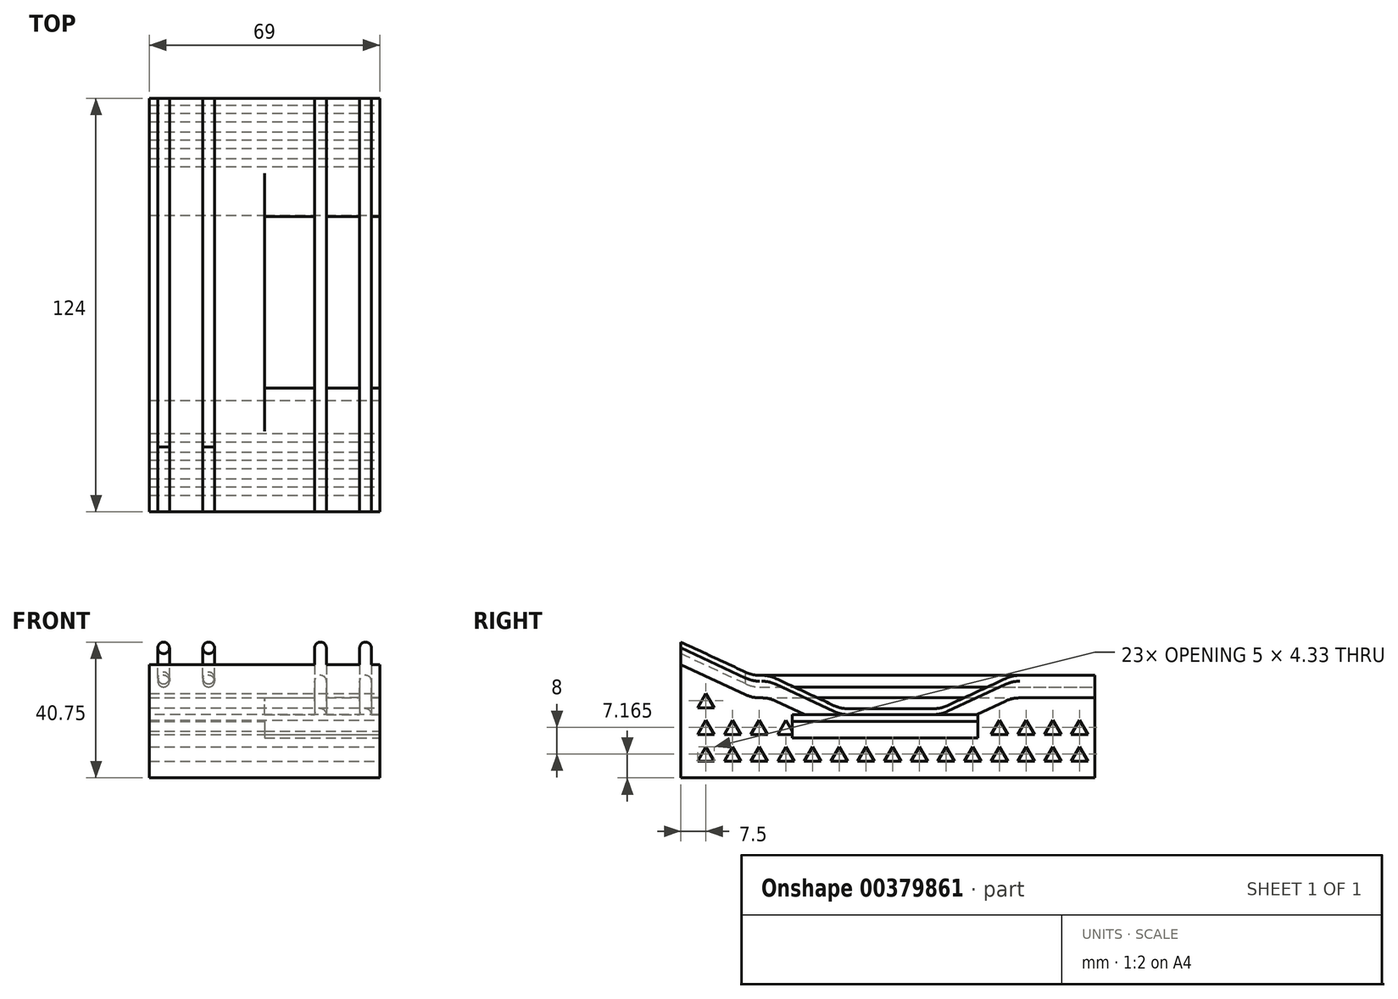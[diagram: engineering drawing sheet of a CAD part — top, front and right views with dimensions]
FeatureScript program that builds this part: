
annotation { "Feature Type Name" : "Feature", "Feature Type Description" : "" }
export const myFeature = defineFeature(function(context is Context, id is Id, definition is map)
    precondition{}
    {
        {
            var Q0;
            Q0=qCreatedBy(makeId("Front.planeOp"),FACE);
            var sketch = newSketch(context, id + "F0", { "sketchPlane" : qUnion([Q0])});
            skLineSegment(sketch, "E0.bottom", {"start": v(-34.5, 10) * mm, "end": v(34.5, 10) * mm});
            skLineSegment(sketch, "E0.top", {"start": v(-34.5, 0) * mm, "end": v(34.5, 0) * mm});
            skLineSegment(sketch, "E0.left", {"start": v(-34.5, 10) * mm, "end": v(-34.5, 0) * mm});
            skLineSegment(sketch, "E0.right", {"start": v(34.5, 10) * mm, "end": v(34.5, 0) * mm});
            skLineSegment(sketch, "E1.bottom", {"start": v(-32, 10) * mm, "end": v(-28.5, 10) * mm});
            skLineSegment(sketch, "E1.top", {"start": v(-32, 15) * mm, "end": v(-28.5, 15) * mm});
            skLineSegment(sketch, "E1.left", {"start": v(-32, 10) * mm, "end": v(-32, 15) * mm});
            skLineSegment(sketch, "E1.right", {"start": v(-28.5, 10) * mm, "end": v(-28.5, 15) * mm});
            skLineSegment(sketch, "E2.bottom", {"start": v(-18.5, 10) * mm, "end": v(-15, 10) * mm});
            skLineSegment(sketch, "E2.top", {"start": v(-18.5, 15) * mm, "end": v(-15, 15) * mm});
            skLineSegment(sketch, "E2.left", {"start": v(-18.5, 10) * mm, "end": v(-18.5, 15) * mm});
            skLineSegment(sketch, "E2.right", {"start": v(-15, 10) * mm, "end": v(-15, 15) * mm});
            skLineSegment(sketch, "E3.MirrorCS", {"start": v(15, 10) * mm, "end": v(15, 15) * mm});
            skLineSegment(sketch, "E4.MirrorCS", {"start": v(18.5, 15) * mm, "end": v(15, 15) * mm});
            skLineSegment(sketch, "E5.MirrorCS", {"start": v(18.5, 10) * mm, "end": v(18.5, 15) * mm});
            skLineSegment(sketch, "E6.MirrorCS", {"start": v(28.5, 10) * mm, "end": v(28.5, 15) * mm});
            skLineSegment(sketch, "E7.MirrorCS", {"start": v(32, 15) * mm, "end": v(28.5, 15) * mm});
            skLineSegment(sketch, "E8.MirrorCS", {"start": v(32, 10) * mm, "end": v(32, 15) * mm});
            skCircle(sketch, "E9", {"center": v(-30.25, 15) * mm, "radius": 1.75 * mm});
            skCircle(sketch, "E10", {"center": v(-16.75, 15) * mm, "radius": 1.75 * mm});
            skCircle(sketch, "E11.MirrorC", {"center": v(16.75, 15) * mm, "radius": 1.75 * mm});
            skCircle(sketch, "E12.MirrorC", {"center": v(30.25, 15) * mm, "radius": 1.75 * mm});
            skLineSegment(sketch, "E13.top", {"start": v(-34.5, -24) * mm, "end": v(34.5, -24) * mm});
            skLineSegment(sketch, "E13.left", {"start": v(-34.5, 0) * mm, "end": v(-34.5, -24) * mm});
            skLineSegment(sketch, "E13.right", {"start": v(34.5, 0) * mm, "end": v(34.5, -24) * mm});
            skLineSegment(sketch, "E14", {"start": v(0, 0) * mm, "end": v(0, 10) * mm});
            skLineSegment(sketch, "E15", {"start": v(34.5, -5) * mm, "end": v(-34.5, -5) * mm});
            skLineSegment(sketch, "E16", {"start": v(-34.5, -12) * mm, "end": v(34.5, -12) * mm});
            skLineSegment(sketch, "E17", {"start": v(-34.5, -7) * mm, "end": v(0, -7) * mm});
            skLineSegment(sketch, "E18", {"start": v(0, -7) * mm, "end": v(0, -12) * mm});
            skSolve(sketch);
        }
        {
            var Q0;
            Q0=qCreatedBy(makeId("Right.planeOp"),FACE);
            var sketch = newSketch(context, id + "F1", { "sketchPlane" : qUnion([Q0])});
            skLineSegment(sketch, "E19", {"start": v(0, 0) * mm, "end": v(19.44, -9.06) * mm});
            skLineSegment(sketch, "E20", {"start": v(101.55, -10) * mm, "end": v(124, -10) * mm, "construction": true});
            skLineSegment(sketch, "E21", {"start": v(28.45, -10.94) * mm, "end": v(45.88, -19.06) * mm});
            skLineSegment(sketch, "E22", {"start": v(50.1, -20) * mm, "end": v(75.67, -20) * mm});
            skLineSegment(sketch, "E23", {"start": v(79.9, -19.06) * mm, "end": v(97.33, -10.94) * mm});
            skLineSegment(sketch, "E24", {"start": v(124, -10) * mm, "end": v(124, -20) * mm, "construction": true});
            skLineSegment(sketch, "E25.MirrorCS", {"start": v(248, 0) * mm, "end": v(226.55, -10) * mm});
            skLineSegment(sketch, "E26.MirrorCS", {"start": v(221.55, -10) * mm, "end": v(200.1, -20) * mm});
            skLineSegment(sketch, "E27.MirrorCS", {"start": v(170.1, -20) * mm, "end": v(147.37, -9.4) * mm});
            skLineSegment(sketch, "E28.MirrorCS", {"start": v(226.55, -10) * mm, "end": v(124, -10) * mm});
            skLineSegment(sketch, "E29.MirrorCS", {"start": v(200.1, -20) * mm, "end": v(170.1, -20) * mm});
            skLineSegment(sketch, "E30", {"start": v(23.66, -10) * mm, "end": v(24.23, -10) * mm});
            skLineSegment(sketch, "E31", {"start": v(101.55, -10) * mm, "end": v(124, -10) * mm});
            skPoint(sketch, "E32.visualSharp", {"position": v(26.45, -10) * mm});
            skArc(sketch, "E32.filletArc", {"start": v(28.45, -10.94) * mm, "mid": v(26.4, -10.24) * mm, "end": v(24.23, -10) * mm});
            skPoint(sketch, "E33.visualSharp", {"position": v(21.45, -10) * mm});
            skArc(sketch, "E33.filletArc", {"start": v(19.44, -9.06) * mm, "mid": v(21.5, -9.76) * mm, "end": v(23.66, -10) * mm});
            skPoint(sketch, "E34.visualSharp", {"position": v(47.9, -20) * mm});
            skArc(sketch, "E34.filletArc", {"start": v(45.88, -19.06) * mm, "mid": v(47.94, -19.76) * mm, "end": v(50.1, -20) * mm});
            skPoint(sketch, "E35.visualSharp", {"position": v(77.9, -20) * mm});
            skArc(sketch, "E35.filletArc", {"start": v(75.67, -20) * mm, "mid": v(77.84, -19.76) * mm, "end": v(79.9, -19.06) * mm});
            skLineSegment(sketch, "E36", {"start": v(24.23, -10) * mm, "end": v(124, -10) * mm});
            skArc(sketch, "E37.filletArc", {"start": v(101.55, -10) * mm, "mid": v(99.39, -10.24) * mm, "end": v(97.33, -10.94) * mm});
            skSolve(sketch);
        }
        {
            var Q0;
            {var subQ0=sQuery(id+"F0.wireOp",EDGE,"E0.left");Q0=makeQuery(id+"F0.imprint","IMPRINT",FACE,{"disambiguationData":[TD([[makeQuery(id+"F0.imprint","IMPRINT",EDGE,{"derivedFrom":subQ0}),1.0]])]});}
            var Q1;
            Q1=makeQuery(id+"F0.imprint","IMPRINT",FACE,{"disambiguationData":[TD([[makeQuery(id+"F0.imprint","IMPRINT",EDGE,{"derivedFrom":sQuery(id+"F0.wireOp",EDGE,"E1.bottom")}),1.0]])]});
            var Q2;
            Q2=makeQuery(id+"F0.imprint","IMPRINT",FACE,{"disambiguationData":[TD([[makeQuery(id+"F0.imprint","IMPRINT",EDGE,{"derivedFrom":sQuery(id+"F0.wireOp",EDGE,"E2.bottom")}),1.0]])]});
            var Q3;
            {var subQ0=sQuery(id+"F0.wireOp",EDGE,"E1.top");Q3=makeQuery(id+"F0.imprint","IMPRINT",FACE,{"disambiguationData":[TD([[makeQuery(id+"F0.imprint","IMPRINT",EDGE,{"derivedFrom":subQ0}),1.0]])]});}
            var Q4;
            {var subQ0=sQuery(id+"F0.wireOp",EDGE,"E2.top");Q4=makeQuery(id+"F0.imprint","IMPRINT",FACE,{"disambiguationData":[TD([[makeQuery(id+"F0.imprint","IMPRINT",EDGE,{"derivedFrom":subQ0}),1.0]])]});}
            var Q5;
            {var subQ0=sQuery(id+"F0.wireOp",EDGE,"E1.top");Q5=makeQuery(id+"F0.imprint","IMPRINT",FACE,{"disambiguationData":[TD([[makeQuery(id+"F0.imprint","IMPRINT",EDGE,{"derivedFrom":subQ0}),-1.0]])]});}
            var Q6;
            {var subQ0=sQuery(id+"F0.wireOp",EDGE,"E2.top");Q6=makeQuery(id+"F0.imprint","IMPRINT",FACE,{"disambiguationData":[TD([[makeQuery(id+"F0.imprint","IMPRINT",EDGE,{"derivedFrom":subQ0}),-1.0]])]});}
            var Q7;
            Q7=sQuery(id+"F1.wireOp",EDGE,"E19");
            var Q8;
            Q8=sQuery(id+"F1.wireOp",EDGE,"E33.filletArc");
            var Q9;
            Q9=sQuery(id+"F1.wireOp",EDGE,"E30");
            var Q10;
            Q10=sQuery(id+"F1.wireOp",EDGE,"E36");
            sweep(context, id + "F2", {"profiles" : qUnion([Q0, Q1, Q2, Q3, Q4, Q5, Q6]), "path" : qUnion([Q7, Q8, Q9, Q10]), "keepProfileOrientation" : true});
        }
        {
            var Q0;
            {var subQ0=sQuery(id+"F0.wireOp",EDGE,"E4.MirrorCS");Q0=makeQuery(id+"F0.imprint","IMPRINT",FACE,{"disambiguationData":[TD([[makeQuery(id+"F0.imprint","IMPRINT",EDGE,{"derivedFrom":subQ0}),-1.0]])]});}
            var Q1;
            {var subQ0=sQuery(id+"F0.wireOp",EDGE,"E7.MirrorCS");Q1=makeQuery(id+"F0.imprint","IMPRINT",FACE,{"disambiguationData":[TD([[makeQuery(id+"F0.imprint","IMPRINT",EDGE,{"derivedFrom":subQ0}),-1.0]])]});}
            var Q2;
            {var subQ0=sQuery(id+"F0.wireOp",EDGE,"E3.MirrorCS");Q2=makeQuery(id+"F0.imprint","IMPRINT",FACE,{"disambiguationData":[TD([[makeQuery(id+"F0.imprint","IMPRINT",EDGE,{"derivedFrom":subQ0}),-1.0]])]});}
            var Q3;
            {var subQ0=sQuery(id+"F0.wireOp",EDGE,"E6.MirrorCS");Q3=makeQuery(id+"F0.imprint","IMPRINT",FACE,{"disambiguationData":[TD([[makeQuery(id+"F0.imprint","IMPRINT",EDGE,{"derivedFrom":subQ0}),-1.0]])]});}
            var Q4;
            {var subQ0=sQuery(id+"F0.wireOp",EDGE,"E4.MirrorCS");Q4=makeQuery(id+"F0.imprint","IMPRINT",FACE,{"disambiguationData":[TD([[makeQuery(id+"F0.imprint","IMPRINT",EDGE,{"derivedFrom":subQ0}),1.0]])]});}
            var Q5;
            {var subQ0=sQuery(id+"F0.wireOp",EDGE,"E7.MirrorCS");Q5=makeQuery(id+"F0.imprint","IMPRINT",FACE,{"disambiguationData":[TD([[makeQuery(id+"F0.imprint","IMPRINT",EDGE,{"derivedFrom":subQ0}),1.0]])]});}
            var Q6;
            {var subQ6=sQuery(id+"F0.wireOp",EDGE,"E0.right");Q6=makeQuery(id+"F0.imprint","IMPRINT",FACE,{"disambiguationData":[TD([[makeQuery(id+"F0.imprint","IMPRINT",EDGE,{"derivedFrom":subQ6}),-1.0]])]});}
            var Q7;
            Q7=sQuery(id+"F1.wireOp",EDGE,"E19");
            var Q8;
            Q8=sQuery(id+"F1.wireOp",EDGE,"E33.filletArc");
            var Q9;
            Q9=sQuery(id+"F1.wireOp",EDGE,"E30");
            var Q10;
            Q10=sQuery(id+"F1.wireOp",EDGE,"E32.filletArc");
            var Q11;
            Q11=sQuery(id+"F1.wireOp",EDGE,"E21");
            var Q12;
            Q12=sQuery(id+"F1.wireOp",EDGE,"E34.filletArc");
            sweep(context, id + "F3", {"operationType" : NewBodyOperationType.ADD, "profiles" : qUnion([Q0, Q1, Q2, Q3, Q4, Q5, Q6]), "path" : qUnion([Q7, Q8, Q9, Q10, Q11, Q12]), "keepProfileOrientation" : true});
        }
        {
            var Q0;
            Q0=makeQuery(id+"F3.opSweep","CAP_FACE",FACE,{"disambiguationData":[OSD([sQuery(id+"F0.wireOp",EDGE,"E0.bottom"),sQuery(id+"F0.wireOp",EDGE,"E0.right"),sQuery(id+"F0.wireOp",EDGE,"E3.MirrorCS"),sQuery(id+"F0.wireOp",EDGE,"E5.MirrorCS"),sQuery(id+"F0.wireOp",EDGE,"E6.MirrorCS"),sQuery(id+"F0.wireOp",EDGE,"E8.MirrorCS"),sQuery(id+"F0.wireOp",EDGE,"E11.MirrorC"),sQuery(id+"F0.wireOp",EDGE,"E12.MirrorC"),sQuery(id+"F0.wireOp",EDGE,"E0.top"),sQuery(id+"F0.wireOp",EDGE,"E14"),sQuery(id+"F1.wireOp",VERTEX,"E34.filletArc.end")])],"isStart":false});
            var Q1;
            Q1=sQuery(id+"F1.wireOp",EDGE,"E22");
            var Q2;
            Q2=sQuery(id+"F1.wireOp",EDGE,"E35.filletArc");
            var Q3;
            Q3=sQuery(id+"F1.wireOp",EDGE,"E23");
            var Q4;
            Q4=sQuery(id+"F1.wireOp",EDGE,"E31");
            var Q5;
            Q5=sQuery(id+"F1.wireOp",EDGE,"E37.filletArc");
            sweep(context, id + "F4", {"profiles" : qUnion([Q0]), "path" : qUnion([Q1, Q2, Q3, Q4, Q5]), "keepProfileOrientation" : true});
        }
        {
            var Q0;
            Q0=makeQuery(id+"F0.imprint","IMPRINT",FACE,{"disambiguationData":[TD([[makeQuery(id+"F0.imprint","IMPRINT",EDGE,{"derivedFrom":sQuery(id+"F0.wireOp",EDGE,"E13.top")}),1.0]])]});
            var Q1;
            {var subQ0=sQuery(id+"F0.wireOp",EDGE,"E15");Q1=makeQuery(id+"F0.imprint","IMPRINT",FACE,{"disambiguationData":[TD([[makeQuery(id+"F0.imprint","IMPRINT",EDGE,{"derivedFrom":subQ0}),1.0]])]});}
            var Q2;
            {var subQ3=sQuery(id+"F0.wireOp",EDGE,"E17");Q2=makeQuery(id+"F0.imprint","IMPRINT",FACE,{"disambiguationData":[TD([[makeQuery(id+"F0.imprint","IMPRINT",EDGE,{"derivedFrom":subQ3}),-1.0]])]});}
            extrude(context, id + "F5", {"entities" : qUnion([Q0, Q1, Q2]), "oppositeDirection" : true, "depth" : 124 * mm});
        }
        {
            var Q0;
            {var subQ0=sQuery(id+"F0.wireOp",EDGE,"E15");Q0=makeQuery(id+"F0.imprint","IMPRINT",FACE,{"disambiguationData":[TD([[makeQuery(id+"F0.imprint","IMPRINT",EDGE,{"derivedFrom":subQ0}),1.0]])]});}
            extrude(context, id + "F6", {"entities" : qUnion([Q0]), "operationType" : NewBodyOperationType.REMOVE, "oppositeDirection" : true, "depth" : 89 * mm});
        }
        {
            var Q0;
            {var subQ0=sQuery(id+"F0.wireOp",EDGE,"E15");Q0=makeQuery(id+"F0.imprint","IMPRINT",FACE,{"disambiguationData":[TD([[makeQuery(id+"F0.imprint","IMPRINT",EDGE,{"derivedFrom":subQ0}),1.0]])]});}
            extrude(context, id + "F7", {"entities" : qUnion([Q0]), "operationType" : NewBodyOperationType.ADD, "oppositeDirection" : true, "depth" : 33.4 * mm});
        }
        {
            var Q0;
            {var subQ3=sQuery(id+"F0.wireOp",EDGE,"E15");Q0=makeQuery(id+"F0.imprint","IMPRINT",FACE,{"disambiguationData":[TD([[makeQuery(id+"F0.imprint","IMPRINT",EDGE,{"derivedFrom":subQ3}),-1.0]])]});}
            extrude(context, id + "F8", {"entities" : qUnion([Q0]), "operationType" : NewBodyOperationType.ADD, "oppositeDirection" : true, "depth" : 15 * mm});
        }
        {
            var Q0;
            Q0=makeQuery(id+"F2.opSweep","SWEPT_BODY",BODY,{"disambiguationData":[OSD([sQuery(id+"F0.wireOp",EDGE,"E0.bottom"),sQuery(id+"F0.wireOp",EDGE,"E0.left"),sQuery(id+"F0.wireOp",EDGE,"E1.left"),sQuery(id+"F0.wireOp",EDGE,"E1.right"),sQuery(id+"F0.wireOp",EDGE,"E2.left"),sQuery(id+"F0.wireOp",EDGE,"E2.right"),sQuery(id+"F0.wireOp",EDGE,"E9"),sQuery(id+"F0.wireOp",EDGE,"E10"),sQuery(id+"F0.wireOp",EDGE,"E0.top"),sQuery(id+"F0.wireOp",EDGE,"E14"),sQuery(id+"F1.wireOp",EDGE,"E20")])]});
            var Q1;
            Q1=makeQuery(id+"F5.opExtrude","SWEPT_BODY",BODY,{"disambiguationData":[OSD([sQuery(id+"F0.wireOp",EDGE,"E13.top"),sQuery(id+"F0.wireOp",EDGE,"E13.left"),sQuery(id+"F0.wireOp",EDGE,"E13.right"),sQuery(id+"F0.wireOp",EDGE,"E15")])]});
            var Q2;
            Q2=makeQuery(id+"F4.opSweep","SWEPT_BODY",BODY,{"disambiguationData":[OSD([sQuery(id+"F0.wireOp",EDGE,"E0.bottom"),sQuery(id+"F0.wireOp",EDGE,"E0.right"),sQuery(id+"F0.wireOp",EDGE,"E3.MirrorCS"),sQuery(id+"F0.wireOp",EDGE,"E5.MirrorCS"),sQuery(id+"F0.wireOp",EDGE,"E6.MirrorCS"),sQuery(id+"F0.wireOp",EDGE,"E8.MirrorCS"),sQuery(id+"F0.wireOp",EDGE,"E11.MirrorC"),sQuery(id+"F0.wireOp",EDGE,"E12.MirrorC"),sQuery(id+"F0.wireOp",EDGE,"E0.top"),sQuery(id+"F0.wireOp",EDGE,"E14"),sQuery(id+"F1.wireOp",VERTEX,"E34.filletArc.end"),sQuery(id+"F1.wireOp",EDGE,"E22")])]});
            booleanBodies(context, id + "F9", {"operationType" : BooleanOperationType.UNION, "tools" : qUnion([Q0, Q1, Q2])});
        }
        {
            var Q0;
            {var subQ0=sQuery(id+"F0.wireOp",EDGE,"E13.right");Q0=makeQuery(id+"F9.opBoolean","MERGE",FACE,{"derivedFrom":[makeQuery(id+"Fo5E0ju6kwFAIzG_1.boolean.opBoolean","MERGE",FACE,{"derivedFrom":[makeQuery(id+"F3.opSweep","SWEPT_FACE",FACE,{"disambiguationData":[OSD([sQuery(id+"F0.wireOp",EDGE,"E0.right"),sQuery(id+"F1.wireOp",EDGE,"E19")])]}),makeQuery(id+"Fo5E0ju6kwFAIzG_1.opExtrude","SWEPT_FACE",FACE,{"disambiguationData":[OSD([sQuery(id+"FUxDlczvYnfELys.wireOp",EDGE,"94261386-e1e3-4ee6-9ad5-568f97032458.right")])]})]}),makeQuery(id+"F8.boolean.opBoolean","MERGE",FACE,{"derivedFrom":[makeQuery(id+"F7.boolean.opBoolean","MERGE",FACE,{"derivedFrom":[makeQuery(id+"F5.opExtrude","SWEPT_FACE",FACE,{"disambiguationData":[OSD([subQ0])]}),makeQuery(id+"F7.opExtrude","SWEPT_FACE",FACE,{"disambiguationData":[OSD([subQ0])]})]}),makeQuery(id+"F8.opExtrude","SWEPT_FACE",FACE,{"disambiguationData":[OSD([subQ0])]})]})]});}
            var sketch = newSketch(context, id + "F10", { "sketchPlane" : qUnion([Q0])});
            skLineSegment(sketch, "E38", {"start": v(5, -19) * mm, "end": v(7.5, -14.67) * mm});
            skLineSegment(sketch, "E39", {"start": v(7.5, -14.67) * mm, "end": v(10, -19) * mm});
            skLineSegment(sketch, "E40", {"start": v(10, -19) * mm, "end": v(5, -19) * mm});
            skLineSegment(sketch, "E41.0.1.0", {"start": v(5, -11) * mm, "end": v(7.5, -6.67) * mm});
            skLineSegment(sketch, "E41.0.1.1", {"start": v(7.5, -6.67) * mm, "end": v(10, -11) * mm});
            skLineSegment(sketch, "E41.0.1.2", {"start": v(10, -11) * mm, "end": v(5, -11) * mm});
            skLineSegment(sketch, "E41.0.2.0", {"start": v(5, -3) * mm, "end": v(7.5, 1.33) * mm});
            skLineSegment(sketch, "E41.0.2.1", {"start": v(7.5, 1.33) * mm, "end": v(10, -3) * mm});
            skLineSegment(sketch, "E41.0.2.2", {"start": v(10, -3) * mm, "end": v(5, -3) * mm});
            skLineSegment(sketch, "E41.1.0.0", {"start": v(13, -19) * mm, "end": v(15.5, -14.67) * mm});
            skLineSegment(sketch, "E41.1.0.1", {"start": v(15.5, -14.67) * mm, "end": v(18, -19) * mm});
            skLineSegment(sketch, "E41.1.0.2", {"start": v(18, -19) * mm, "end": v(13, -19) * mm});
            skLineSegment(sketch, "E41.1.1.0", {"start": v(13, -11) * mm, "end": v(15.5, -6.67) * mm});
            skLineSegment(sketch, "E41.1.1.1", {"start": v(15.5, -6.67) * mm, "end": v(18, -11) * mm});
            skLineSegment(sketch, "E41.1.1.2", {"start": v(18, -11) * mm, "end": v(13, -11) * mm});
            skLineSegment(sketch, "E41.1.2.0", {"start": v(13, -3) * mm, "end": v(15.5, 1.33) * mm});
            skLineSegment(sketch, "E41.1.2.1", {"start": v(15.5, 1.33) * mm, "end": v(18, -3) * mm});
            skLineSegment(sketch, "E41.1.2.2", {"start": v(18, -3) * mm, "end": v(13, -3) * mm});
            skLineSegment(sketch, "E41.2.0.0", {"start": v(21, -19) * mm, "end": v(23.5, -14.67) * mm});
            skLineSegment(sketch, "E41.2.0.1", {"start": v(23.5, -14.67) * mm, "end": v(26, -19) * mm});
            skLineSegment(sketch, "E41.2.0.2", {"start": v(26, -19) * mm, "end": v(21, -19) * mm});
            skLineSegment(sketch, "E41.2.1.0", {"start": v(21, -11) * mm, "end": v(23.5, -6.67) * mm});
            skLineSegment(sketch, "E41.2.1.1", {"start": v(23.5, -6.67) * mm, "end": v(26, -11) * mm});
            skLineSegment(sketch, "E41.2.1.2", {"start": v(26, -11) * mm, "end": v(21, -11) * mm});
            skLineSegment(sketch, "E41.2.2.0", {"start": v(21, -3) * mm, "end": v(23.5, 1.33) * mm});
            skLineSegment(sketch, "E41.2.2.1", {"start": v(23.5, 1.33) * mm, "end": v(26, -3) * mm});
            skLineSegment(sketch, "E41.2.2.2", {"start": v(26, -3) * mm, "end": v(21, -3) * mm});
            skLineSegment(sketch, "E41.3.0.0", {"start": v(29, -19) * mm, "end": v(31.5, -14.67) * mm});
            skLineSegment(sketch, "E41.3.0.1", {"start": v(31.5, -14.67) * mm, "end": v(34, -19) * mm});
            skLineSegment(sketch, "E41.3.0.2", {"start": v(34, -19) * mm, "end": v(29, -19) * mm});
            skLineSegment(sketch, "E41.3.1.0", {"start": v(29, -11) * mm, "end": v(31.5, -6.67) * mm});
            skLineSegment(sketch, "E41.3.1.1", {"start": v(31.5, -6.67) * mm, "end": v(34, -11) * mm});
            skLineSegment(sketch, "E41.3.1.2", {"start": v(34, -11) * mm, "end": v(29, -11) * mm});
            skLineSegment(sketch, "E41.3.2.0", {"start": v(29, -3) * mm, "end": v(31.5, 1.33) * mm});
            skLineSegment(sketch, "E41.3.2.1", {"start": v(31.5, 1.33) * mm, "end": v(34, -3) * mm});
            skLineSegment(sketch, "E41.3.2.2", {"start": v(34, -3) * mm, "end": v(29, -3) * mm});
            skLineSegment(sketch, "E41.4.0.0", {"start": v(37, -19) * mm, "end": v(39.5, -14.67) * mm});
            skLineSegment(sketch, "E41.4.0.1", {"start": v(39.5, -14.67) * mm, "end": v(42, -19) * mm});
            skLineSegment(sketch, "E41.4.0.2", {"start": v(42, -19) * mm, "end": v(37, -19) * mm});
            skLineSegment(sketch, "E41.4.1.0", {"start": v(37, -11) * mm, "end": v(39.5, -6.67) * mm});
            skLineSegment(sketch, "E41.4.1.1", {"start": v(39.5, -6.67) * mm, "end": v(42, -11) * mm});
            skLineSegment(sketch, "E41.4.1.2", {"start": v(42, -11) * mm, "end": v(37, -11) * mm});
            skLineSegment(sketch, "E41.4.2.0", {"start": v(37, -3) * mm, "end": v(39.5, 1.33) * mm});
            skLineSegment(sketch, "E41.4.2.1", {"start": v(39.5, 1.33) * mm, "end": v(42, -3) * mm});
            skLineSegment(sketch, "E41.4.2.2", {"start": v(42, -3) * mm, "end": v(37, -3) * mm});
            skLineSegment(sketch, "E41.5.0.0", {"start": v(45, -19) * mm, "end": v(47.5, -14.67) * mm});
            skLineSegment(sketch, "E41.5.0.1", {"start": v(47.5, -14.67) * mm, "end": v(50, -19) * mm});
            skLineSegment(sketch, "E41.5.0.2", {"start": v(50, -19) * mm, "end": v(45, -19) * mm});
            skLineSegment(sketch, "E41.5.1.0", {"start": v(45, -11) * mm, "end": v(47.5, -6.67) * mm});
            skLineSegment(sketch, "E41.5.1.1", {"start": v(47.5, -6.67) * mm, "end": v(50, -11) * mm});
            skLineSegment(sketch, "E41.5.1.2", {"start": v(50, -11) * mm, "end": v(45, -11) * mm});
            skLineSegment(sketch, "E41.5.2.0", {"start": v(45, -3) * mm, "end": v(47.5, 1.33) * mm});
            skLineSegment(sketch, "E41.5.2.1", {"start": v(47.5, 1.33) * mm, "end": v(50, -3) * mm});
            skLineSegment(sketch, "E41.5.2.2", {"start": v(50, -3) * mm, "end": v(45, -3) * mm});
            skLineSegment(sketch, "E41.6.0.0", {"start": v(53, -19) * mm, "end": v(55.5, -14.67) * mm});
            skLineSegment(sketch, "E41.6.0.1", {"start": v(55.5, -14.67) * mm, "end": v(58, -19) * mm});
            skLineSegment(sketch, "E41.6.0.2", {"start": v(58, -19) * mm, "end": v(53, -19) * mm});
            skLineSegment(sketch, "E41.6.1.0", {"start": v(53, -11) * mm, "end": v(55.5, -6.67) * mm});
            skLineSegment(sketch, "E41.6.1.1", {"start": v(55.5, -6.67) * mm, "end": v(58, -11) * mm});
            skLineSegment(sketch, "E41.6.1.2", {"start": v(58, -11) * mm, "end": v(53, -11) * mm});
            skLineSegment(sketch, "E41.6.2.0", {"start": v(53, -3) * mm, "end": v(55.5, 1.33) * mm});
            skLineSegment(sketch, "E41.6.2.1", {"start": v(55.5, 1.33) * mm, "end": v(58, -3) * mm});
            skLineSegment(sketch, "E41.6.2.2", {"start": v(58, -3) * mm, "end": v(53, -3) * mm});
            skLineSegment(sketch, "E41.7.0.0", {"start": v(61, -19) * mm, "end": v(63.5, -14.67) * mm});
            skLineSegment(sketch, "E41.7.0.1", {"start": v(63.5, -14.67) * mm, "end": v(66, -19) * mm});
            skLineSegment(sketch, "E41.7.0.2", {"start": v(66, -19) * mm, "end": v(61, -19) * mm});
            skLineSegment(sketch, "E41.7.1.0", {"start": v(61, -11) * mm, "end": v(63.5, -6.67) * mm});
            skLineSegment(sketch, "E41.7.1.1", {"start": v(63.5, -6.67) * mm, "end": v(66, -11) * mm});
            skLineSegment(sketch, "E41.7.1.2", {"start": v(66, -11) * mm, "end": v(61, -11) * mm});
            skLineSegment(sketch, "E41.7.2.0", {"start": v(61, -3) * mm, "end": v(63.5, 1.33) * mm});
            skLineSegment(sketch, "E41.7.2.1", {"start": v(63.5, 1.33) * mm, "end": v(66, -3) * mm});
            skLineSegment(sketch, "E41.7.2.2", {"start": v(66, -3) * mm, "end": v(61, -3) * mm});
            skLineSegment(sketch, "E41.8.0.0", {"start": v(69, -19) * mm, "end": v(71.5, -14.67) * mm});
            skLineSegment(sketch, "E41.8.0.1", {"start": v(71.5, -14.67) * mm, "end": v(74, -19) * mm});
            skLineSegment(sketch, "E41.8.0.2", {"start": v(74, -19) * mm, "end": v(69, -19) * mm});
            skLineSegment(sketch, "E41.8.1.0", {"start": v(69, -11) * mm, "end": v(71.5, -6.67) * mm});
            skLineSegment(sketch, "E41.8.1.1", {"start": v(71.5, -6.67) * mm, "end": v(74, -11) * mm});
            skLineSegment(sketch, "E41.8.1.2", {"start": v(74, -11) * mm, "end": v(69, -11) * mm});
            skLineSegment(sketch, "E41.8.2.0", {"start": v(69, -3) * mm, "end": v(71.5, 1.33) * mm});
            skLineSegment(sketch, "E41.8.2.1", {"start": v(71.5, 1.33) * mm, "end": v(74, -3) * mm});
            skLineSegment(sketch, "E41.8.2.2", {"start": v(74, -3) * mm, "end": v(69, -3) * mm});
            skLineSegment(sketch, "E41.9.0.0", {"start": v(77, -19) * mm, "end": v(79.5, -14.67) * mm});
            skLineSegment(sketch, "E41.9.0.1", {"start": v(79.5, -14.67) * mm, "end": v(82, -19) * mm});
            skLineSegment(sketch, "E41.9.0.2", {"start": v(82, -19) * mm, "end": v(77, -19) * mm});
            skLineSegment(sketch, "E41.9.1.0", {"start": v(77, -11) * mm, "end": v(79.5, -6.67) * mm});
            skLineSegment(sketch, "E41.9.1.1", {"start": v(79.5, -6.67) * mm, "end": v(82, -11) * mm});
            skLineSegment(sketch, "E41.9.1.2", {"start": v(82, -11) * mm, "end": v(77, -11) * mm});
            skLineSegment(sketch, "E41.9.2.0", {"start": v(77, -3) * mm, "end": v(79.5, 1.33) * mm});
            skLineSegment(sketch, "E41.9.2.1", {"start": v(79.5, 1.33) * mm, "end": v(82, -3) * mm});
            skLineSegment(sketch, "E41.9.2.2", {"start": v(82, -3) * mm, "end": v(77, -3) * mm});
            skLineSegment(sketch, "E41.10.0.0", {"start": v(85, -19) * mm, "end": v(87.5, -14.67) * mm});
            skLineSegment(sketch, "E41.10.0.1", {"start": v(87.5, -14.67) * mm, "end": v(90, -19) * mm});
            skLineSegment(sketch, "E41.10.0.2", {"start": v(90, -19) * mm, "end": v(85, -19) * mm});
            skLineSegment(sketch, "E41.10.1.0", {"start": v(85, -11) * mm, "end": v(87.5, -6.67) * mm});
            skLineSegment(sketch, "E41.10.1.1", {"start": v(87.5, -6.67) * mm, "end": v(90, -11) * mm});
            skLineSegment(sketch, "E41.10.1.2", {"start": v(90, -11) * mm, "end": v(85, -11) * mm});
            skLineSegment(sketch, "E41.10.2.0", {"start": v(85, -3) * mm, "end": v(87.5, 1.33) * mm});
            skLineSegment(sketch, "E41.10.2.1", {"start": v(87.5, 1.33) * mm, "end": v(90, -3) * mm});
            skLineSegment(sketch, "E41.10.2.2", {"start": v(90, -3) * mm, "end": v(85, -3) * mm});
            skLineSegment(sketch, "E41.11.0.0", {"start": v(93, -19) * mm, "end": v(95.5, -14.67) * mm});
            skLineSegment(sketch, "E41.11.0.1", {"start": v(95.5, -14.67) * mm, "end": v(98, -19) * mm});
            skLineSegment(sketch, "E41.11.0.2", {"start": v(98, -19) * mm, "end": v(93, -19) * mm});
            skLineSegment(sketch, "E41.11.1.0", {"start": v(93, -11) * mm, "end": v(95.5, -6.67) * mm});
            skLineSegment(sketch, "E41.11.1.1", {"start": v(95.5, -6.67) * mm, "end": v(98, -11) * mm});
            skLineSegment(sketch, "E41.11.1.2", {"start": v(98, -11) * mm, "end": v(93, -11) * mm});
            skLineSegment(sketch, "E41.11.2.0", {"start": v(93, -3) * mm, "end": v(95.5, 1.33) * mm});
            skLineSegment(sketch, "E41.11.2.1", {"start": v(95.5, 1.33) * mm, "end": v(98, -3) * mm});
            skLineSegment(sketch, "E41.11.2.2", {"start": v(98, -3) * mm, "end": v(93, -3) * mm});
            skLineSegment(sketch, "E41.12.0.0", {"start": v(101, -19) * mm, "end": v(103.5, -14.67) * mm});
            skLineSegment(sketch, "E41.12.0.1", {"start": v(103.5, -14.67) * mm, "end": v(106, -19) * mm});
            skLineSegment(sketch, "E41.12.0.2", {"start": v(106, -19) * mm, "end": v(101, -19) * mm});
            skLineSegment(sketch, "E41.12.1.0", {"start": v(101, -11) * mm, "end": v(103.5, -6.67) * mm});
            skLineSegment(sketch, "E41.12.1.1", {"start": v(103.5, -6.67) * mm, "end": v(106, -11) * mm});
            skLineSegment(sketch, "E41.12.1.2", {"start": v(106, -11) * mm, "end": v(101, -11) * mm});
            skLineSegment(sketch, "E41.12.2.0", {"start": v(101, -3) * mm, "end": v(103.5, 1.33) * mm});
            skLineSegment(sketch, "E41.12.2.1", {"start": v(103.5, 1.33) * mm, "end": v(106, -3) * mm});
            skLineSegment(sketch, "E41.12.2.2", {"start": v(106, -3) * mm, "end": v(101, -3) * mm});
            skLineSegment(sketch, "E41.13.0.0", {"start": v(109, -19) * mm, "end": v(111.5, -14.67) * mm});
            skLineSegment(sketch, "E41.13.0.1", {"start": v(111.5, -14.67) * mm, "end": v(114, -19) * mm});
            skLineSegment(sketch, "E41.13.0.2", {"start": v(114, -19) * mm, "end": v(109, -19) * mm});
            skLineSegment(sketch, "E41.13.1.0", {"start": v(109, -11) * mm, "end": v(111.5, -6.67) * mm});
            skLineSegment(sketch, "E41.13.1.1", {"start": v(111.5, -6.67) * mm, "end": v(114, -11) * mm});
            skLineSegment(sketch, "E41.13.1.2", {"start": v(114, -11) * mm, "end": v(109, -11) * mm});
            skLineSegment(sketch, "E41.13.2.0", {"start": v(109, -3) * mm, "end": v(111.5, 1.33) * mm});
            skLineSegment(sketch, "E41.13.2.1", {"start": v(111.5, 1.33) * mm, "end": v(114, -3) * mm});
            skLineSegment(sketch, "E41.13.2.2", {"start": v(114, -3) * mm, "end": v(109, -3) * mm});
            skLineSegment(sketch, "E41.14.0.0", {"start": v(117, -19) * mm, "end": v(119.5, -14.67) * mm});
            skLineSegment(sketch, "E41.14.0.1", {"start": v(119.5, -14.67) * mm, "end": v(122, -19) * mm});
            skLineSegment(sketch, "E41.14.0.2", {"start": v(122, -19) * mm, "end": v(117, -19) * mm});
            skLineSegment(sketch, "E41.14.1.0", {"start": v(117, -11) * mm, "end": v(119.5, -6.67) * mm});
            skLineSegment(sketch, "E41.14.1.1", {"start": v(119.5, -6.67) * mm, "end": v(122, -11) * mm});
            skLineSegment(sketch, "E41.14.1.2", {"start": v(122, -11) * mm, "end": v(117, -11) * mm});
            skLineSegment(sketch, "E41.14.2.0", {"start": v(117, -3) * mm, "end": v(119.5, 1.33) * mm});
            skLineSegment(sketch, "E41.14.2.1", {"start": v(119.5, 1.33) * mm, "end": v(122, -3) * mm});
            skLineSegment(sketch, "E41.14.2.2", {"start": v(122, -3) * mm, "end": v(117, -3) * mm});
            skLineSegment(sketch, "E41.direction1", {"start": v(5, -19) * mm, "end": v(13, -19) * mm, "construction": true});
            skLineSegment(sketch, "E41.direction2", {"start": v(5, -19) * mm, "end": v(5, -11) * mm, "construction": true});
            skSolve(sketch);
        }
        {
            var Q0;
            Q0=makeQuery(id+"F10.imprint","IMPRINT",FACE,{"disambiguationData":[TD([[makeQuery(id+"F10.imprint","IMPRINT",EDGE,{"derivedFrom":sQuery(id+"F10.wireOp",EDGE,"E41.0.1.0")}),-1.0]])]});
            var Q1;
            Q1=makeQuery(id+"F10.imprint","IMPRINT",FACE,{"disambiguationData":[TD([[makeQuery(id+"F10.imprint","IMPRINT",EDGE,{"derivedFrom":sQuery(id+"F10.wireOp",EDGE,"E41.0.2.0")}),-1.0]])]});
            var Q2;
            Q2=makeQuery(id+"F10.imprint","IMPRINT",FACE,{"disambiguationData":[TD([[makeQuery(id+"F10.imprint","IMPRINT",EDGE,{"derivedFrom":sQuery(id+"F10.wireOp",EDGE,"E38")}),-1.0]])]});
            var Q3;
            Q3=makeQuery(id+"F10.imprint","IMPRINT",FACE,{"disambiguationData":[TD([[makeQuery(id+"F10.imprint","IMPRINT",EDGE,{"derivedFrom":sQuery(id+"F10.wireOp",EDGE,"E41.1.0.0")}),-1.0]])]});
            var Q4;
            Q4=makeQuery(id+"F10.imprint","IMPRINT",FACE,{"disambiguationData":[TD([[makeQuery(id+"F10.imprint","IMPRINT",EDGE,{"derivedFrom":sQuery(id+"F10.wireOp",EDGE,"E41.1.1.0")}),-1.0]])]});
            var Q5;
            Q5=makeQuery(id+"F10.imprint","IMPRINT",FACE,{"disambiguationData":[TD([[makeQuery(id+"F10.imprint","IMPRINT",EDGE,{"derivedFrom":sQuery(id+"F10.wireOp",EDGE,"E41.2.0.0")}),-1.0]])]});
            var Q6;
            Q6=makeQuery(id+"F10.imprint","IMPRINT",FACE,{"disambiguationData":[TD([[makeQuery(id+"F10.imprint","IMPRINT",EDGE,{"derivedFrom":sQuery(id+"F10.wireOp",EDGE,"E41.2.1.0")}),-1.0]])]});
            var Q7;
            Q7=makeQuery(id+"F10.imprint","IMPRINT",FACE,{"disambiguationData":[TD([[makeQuery(id+"F10.imprint","IMPRINT",EDGE,{"derivedFrom":sQuery(id+"F10.wireOp",EDGE,"E41.3.1.0")}),-1.0]])]});
            var Q8;
            Q8=makeQuery(id+"F10.imprint","IMPRINT",FACE,{"disambiguationData":[TD([[makeQuery(id+"F10.imprint","IMPRINT",EDGE,{"derivedFrom":sQuery(id+"F10.wireOp",EDGE,"E41.3.0.0")}),-1.0]])]});
            var Q9;
            Q9=makeQuery(id+"F10.imprint","IMPRINT",FACE,{"disambiguationData":[TD([[makeQuery(id+"F10.imprint","IMPRINT",EDGE,{"derivedFrom":sQuery(id+"F10.wireOp",EDGE,"E41.4.0.0")}),-1.0]])]});
            var Q10;
            Q10=makeQuery(id+"F10.imprint","IMPRINT",FACE,{"disambiguationData":[TD([[makeQuery(id+"F10.imprint","IMPRINT",EDGE,{"derivedFrom":sQuery(id+"F10.wireOp",EDGE,"E41.5.0.0")}),-1.0]])]});
            var Q11;
            Q11=makeQuery(id+"F10.imprint","IMPRINT",FACE,{"disambiguationData":[TD([[makeQuery(id+"F10.imprint","IMPRINT",EDGE,{"derivedFrom":sQuery(id+"F10.wireOp",EDGE,"E41.6.0.0")}),-1.0]])]});
            var Q12;
            Q12=makeQuery(id+"F10.imprint","IMPRINT",FACE,{"disambiguationData":[TD([[makeQuery(id+"F10.imprint","IMPRINT",EDGE,{"derivedFrom":sQuery(id+"F10.wireOp",EDGE,"E41.7.0.0")}),-1.0]])]});
            var Q13;
            Q13=makeQuery(id+"F10.imprint","IMPRINT",FACE,{"disambiguationData":[TD([[makeQuery(id+"F10.imprint","IMPRINT",EDGE,{"derivedFrom":sQuery(id+"F10.wireOp",EDGE,"E41.8.0.0")}),-1.0]])]});
            var Q14;
            Q14=makeQuery(id+"F10.imprint","IMPRINT",FACE,{"disambiguationData":[TD([[makeQuery(id+"F10.imprint","IMPRINT",EDGE,{"derivedFrom":sQuery(id+"F10.wireOp",EDGE,"E41.9.0.0")}),-1.0]])]});
            var Q15;
            Q15=makeQuery(id+"F10.imprint","IMPRINT",FACE,{"disambiguationData":[TD([[makeQuery(id+"F10.imprint","IMPRINT",EDGE,{"derivedFrom":sQuery(id+"F10.wireOp",EDGE,"E41.10.0.0")}),-1.0]])]});
            var Q16;
            Q16=makeQuery(id+"F10.imprint","IMPRINT",FACE,{"disambiguationData":[TD([[makeQuery(id+"F10.imprint","IMPRINT",EDGE,{"derivedFrom":sQuery(id+"F10.wireOp",EDGE,"E41.11.0.0")}),-1.0]])]});
            var Q17;
            Q17=makeQuery(id+"F10.imprint","IMPRINT",FACE,{"disambiguationData":[TD([[makeQuery(id+"F10.imprint","IMPRINT",EDGE,{"derivedFrom":sQuery(id+"F10.wireOp",EDGE,"E41.11.1.0")}),-1.0]])]});
            var Q18;
            Q18=makeQuery(id+"F10.imprint","IMPRINT",FACE,{"disambiguationData":[TD([[makeQuery(id+"F10.imprint","IMPRINT",EDGE,{"derivedFrom":sQuery(id+"F10.wireOp",EDGE,"E41.12.0.0")}),-1.0]])]});
            var Q19;
            Q19=makeQuery(id+"F10.imprint","IMPRINT",FACE,{"disambiguationData":[TD([[makeQuery(id+"F10.imprint","IMPRINT",EDGE,{"derivedFrom":sQuery(id+"F10.wireOp",EDGE,"E41.13.1.0")}),-1.0]])]});
            var Q20;
            Q20=makeQuery(id+"F10.imprint","IMPRINT",FACE,{"disambiguationData":[TD([[makeQuery(id+"F10.imprint","IMPRINT",EDGE,{"derivedFrom":sQuery(id+"F10.wireOp",EDGE,"E41.13.0.0")}),-1.0]])]});
            var Q21;
            Q21=makeQuery(id+"F10.imprint","IMPRINT",FACE,{"disambiguationData":[TD([[makeQuery(id+"F10.imprint","IMPRINT",EDGE,{"derivedFrom":sQuery(id+"F10.wireOp",EDGE,"E41.14.0.0")}),-1.0]])]});
            var Q22;
            Q22=makeQuery(id+"F10.imprint","IMPRINT",FACE,{"disambiguationData":[TD([[makeQuery(id+"F10.imprint","IMPRINT",EDGE,{"derivedFrom":sQuery(id+"F10.wireOp",EDGE,"E41.14.1.0")}),-1.0]])]});
            var Q23;
            Q23=makeQuery(id+"F10.imprint","IMPRINT",FACE,{"disambiguationData":[TD([[makeQuery(id+"F10.imprint","IMPRINT",EDGE,{"derivedFrom":sQuery(id+"F10.wireOp",EDGE,"E41.12.1.0")}),-1.0]])]});
            extrude(context, id + "F11", {"entities" : qUnion([Q0, Q1, Q2, Q3, Q4, Q5, Q6, Q7, Q8, Q9, Q10, Q11, Q12, Q13, Q14, Q15, Q16, Q17, Q18, Q19, Q20, Q21, Q22, Q23]), "operationType" : NewBodyOperationType.REMOVE, "oppositeDirection" : true, "depth" : 77.1 * mm});
        }
    });
